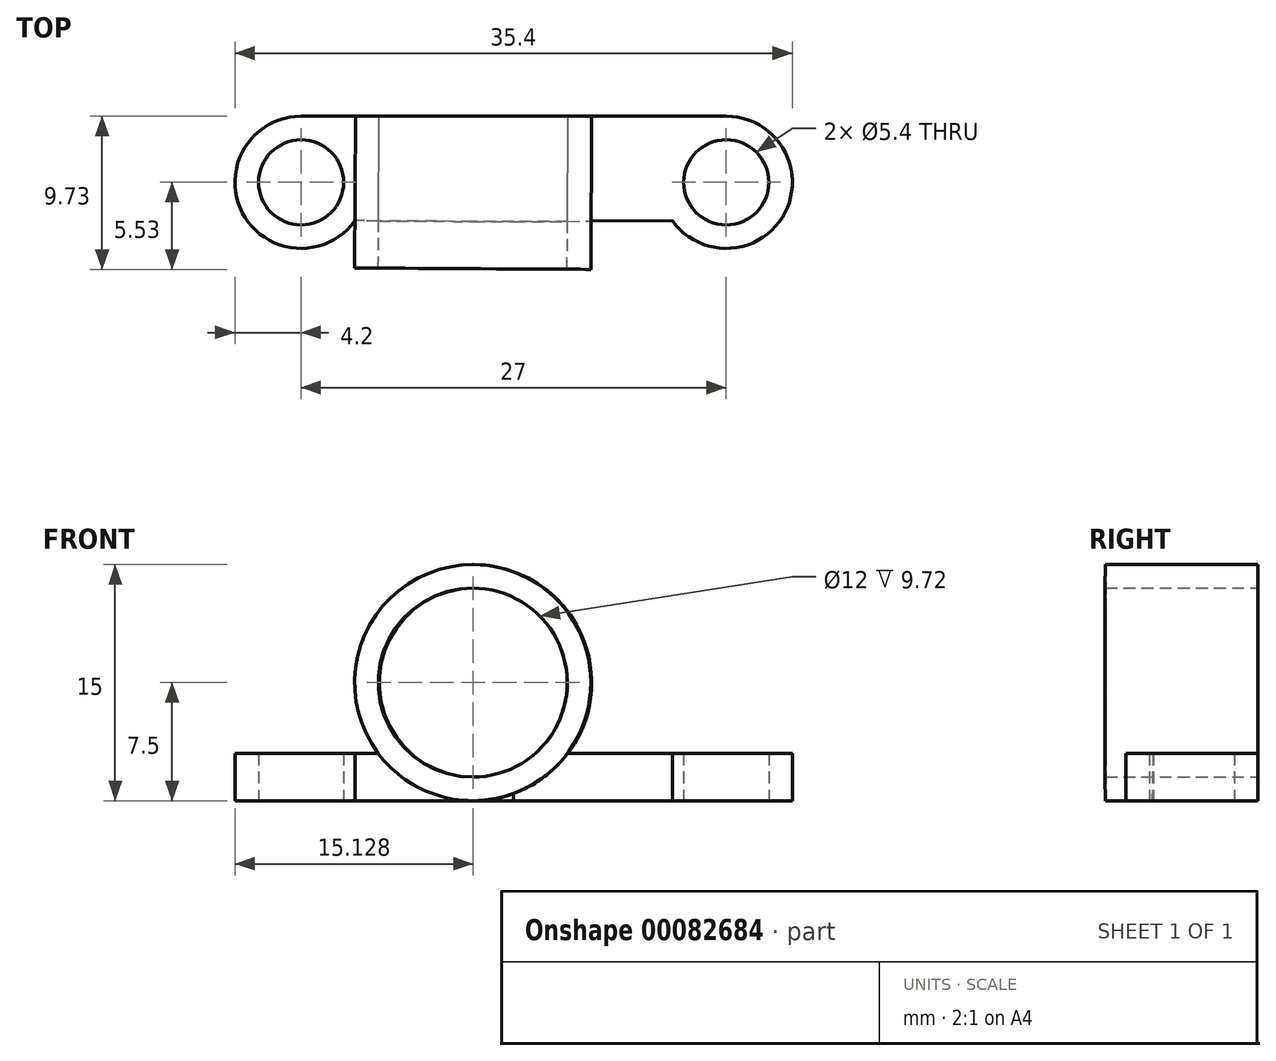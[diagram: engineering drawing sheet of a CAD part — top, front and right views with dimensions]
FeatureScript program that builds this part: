
annotation { "Feature Type Name" : "Feature", "Feature Type Description" : "" }
export const myFeature = defineFeature(function(context is Context, id is Id, definition is map)
    precondition{}
    {
        {
            var Q0;
            Q0=qCreatedBy(makeId("Top.planeOp"),FACE);
            var sketch = newSketch(context, id + "F0", { "sketchPlane" : qUnion([Q0])});
            skLineSegment(sketch, "E0", {"start": v(0, 0) * mm, "end": v(-13.5, 0) * mm, "construction": true});
            skCircle(sketch, "E1", {"center": v(-13.5, 0) * mm, "radius": 2.7 * mm});
            skArc(sketch, "E2", {"start": v(-13.5, 4.2) * mm, "mid": v(-17.23, -1.92) * mm, "end": v(-10.08, -2.44) * mm});
            skLineSegment(sketch, "E3.MirrorCS", {"start": v(0, -2.5) * mm, "end": v(-10.08, -2.44) * mm});
            skLineSegment(sketch, "E4.MirrorCS", {"start": v(0, -2.5) * mm, "end": v(10.08, -2.44) * mm});
            skArc(sketch, "E5.MirrorC", {"start": v(13.5, 4.2) * mm, "mid": v(17.23, -1.92) * mm, "end": v(10.08, -2.44) * mm});
            skCircle(sketch, "E6.MirrorC", {"center": v(13.5, 0) * mm, "radius": 2.7 * mm});
            skLineSegment(sketch, "E7", {"start": v(-13.5, 4.2) * mm, "end": v(13.5, 4.2) * mm});
            skPoint(sketch, "E8.end.orphan", {"position": v(-10.08, 2.44) * mm});
            skPoint(sketch, "E8.start.orphan", {"position": v(0, 2.5) * mm});
            skPoint(sketch, "E9.orphan", {"position": v(10.08, 2.44) * mm});
            skSolve(sketch);
        }
        {
            var Q0;
            Q0=makeQuery(id+"F0.imprint","IMPRINT",FACE,{"disambiguationData":[TD([[makeQuery(id+"F0.imprint","IMPRINT",EDGE,{"derivedFrom":sQuery(id+"F0.wireOp",EDGE,"E1")}),-1.0]])]});
            extrude(context, id + "F1", {"entities" : qUnion([Q0]), "depth" : 3 * mm});
        }
        {
            var Q0;
            Q0=makeQuery(id+"F1.opExtrude","SWEPT_FACE",FACE,{"disambiguationData":[OSD([sQuery(id+"F0.wireOp",EDGE,"E3.MirrorCS"),sQuery(id+"F0.wireOp",EDGE,"E4.MirrorCS")])]});
            var sketch = newSketch(context, id + "F2", { "sketchPlane" : qUnion([Q0])});
            skCircle(sketch, "E10", {"center": v(-2.57, 7.5) * mm, "radius": 6 * mm});
            skCircle(sketch, "E11", {"center": v(-2.57, 7.5) * mm, "radius": 7.5 * mm});
            skSolve(sketch);
        }
        {
            var Q0;
            {var subQ0=sQuery(id+"F2.wireOp",EDGE,"E10");var subQ1=makeQuery(id+"F1.opExtrude","CAP_EDGE",EDGE,{"disambiguationData":[OSD([sQuery(id+"F0.wireOp",EDGE,"E3.MirrorCS"),sQuery(id+"F0.wireOp",EDGE,"E4.MirrorCS")])],"isStart":false});var subQ2=makeQuery(id+"F2.imprint","INTERSECT",VERTEX,{"disambiguationData":[OD(0.0)],"derivedFrom":[subQ1,subQ0]});Q0=makeQuery(id+"F2.imprint","IMPRINT",FACE,{"disambiguationData":[TD([[makeQuery(id+"F2.imprint","IMPRINT",EDGE,{"disambiguationData":[TD([[subQ2,1.0]])],"derivedFrom":subQ0}),-1.0]])]});}
            var Q1;
            {var subQ1=sQuery(id+"F0.wireOp",EDGE,"E4.MirrorCS");var subQ2=sQuery(id+"F0.wireOp",EDGE,"E3.MirrorCS");var subQ3=makeQuery(id+"F1.opExtrude","CAP_EDGE",EDGE,{"disambiguationData":[OSD([subQ2,subQ1])],"isStart":false});var subQ5=sQuery(id+"F2.wireOp",EDGE,"E10");var subQ6=makeQuery(id+"F2.imprint","INTERSECT",VERTEX,{"disambiguationData":[OD(0.0)],"derivedFrom":[subQ3,subQ5]});Q1=makeQuery(id+"F2.imprint","IMPRINT",FACE,{"disambiguationData":[TD([[makeQuery(id+"F2.imprint","IMPRINT",EDGE,{"disambiguationData":[TD([[subQ6,-1.0]])],"derivedFrom":subQ5}),-1.0]])]});}
            var Q2;
            Q2=makeQuery(id+"F1.opExtrude","SWEPT_FACE",FACE,{"disambiguationData":[OSD([sQuery(id+"F0.wireOp",EDGE,"E7")])]});
            extrude(context, id + "F3", {"entities" : qUnion([Q0, Q1]), "operationType" : NewBodyOperationType.ADD, "depth" : 3 * mm, "hasSecondDirection" : true, "secondDirectionBound" : SecondDirectionBoundingType.UP_TO_SURFACE, "secondDirectionOppositeDirection" : true, "secondDirectionBoundEntityFace" : qUnion([Q2]), "secondDirectionDepth" : 5 * mm});
        }
        {
            var Q0;
            {var subQ0=sQuery(id+"F0.wireOp",EDGE,"E4.MirrorCS");var subQ1=sQuery(id+"F0.wireOp",EDGE,"E3.MirrorCS");Q0=makeQuery(id+"F3.boolean.opBoolean","SPLIT",FACE,{"disambiguationData":[TD([makeQuery(id+"F3.opExtrude","SWEPT_FACE",FACE,{"disambiguationData":[OSD([sQuery(id+"F2.wireOp",EDGE,"E10")])]})])],"derivedFrom":makeQuery(id+"F1.opExtrude","SWEPT_FACE",FACE,{"disambiguationData":[OSD([subQ1,subQ0])]})});}
            extrude(context, id + "F4", {"entities" : qUnion([Q0]), "operationType" : NewBodyOperationType.REMOVE, "oppositeDirection" : true, "depth" : 25 * mm});
        }
    });
